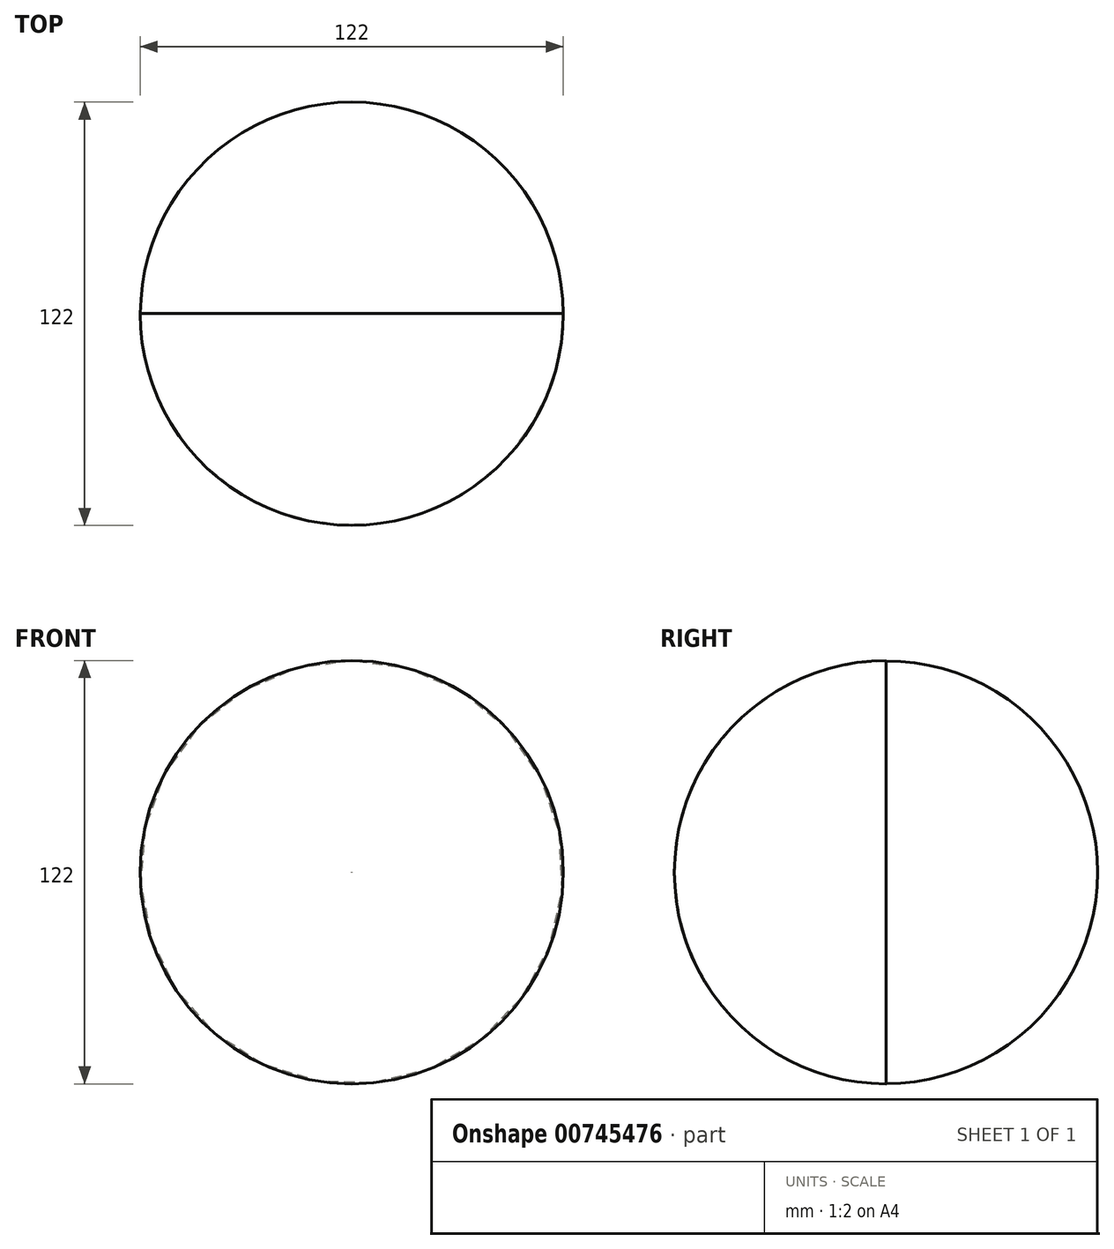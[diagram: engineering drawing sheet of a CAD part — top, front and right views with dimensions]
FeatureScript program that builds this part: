
annotation { "Feature Type Name" : "Feature", "Feature Type Description" : "" }
export const myFeature = defineFeature(function(context is Context, id is Id, definition is map)
    precondition{}
    {
        {
            var Q0;
            Q0=qCreatedBy(makeId("Front.planeOp"),FACE);
            var sketch = newSketch(context, id + "F0", { "sketchPlane" : qUnion([Q0])});
            skCircle(sketch, "E0", {"center": v(0, 0) * mm, "radius": 61 * mm});
            skSolve(sketch);
        }
        {
            var Q0;
            Q0 = qSketchRegion(id + "F0", true);
            extrude(context, id + "F1", {"entities" : qUnion([Q0]), "depth" : 122 * mm, "offsetDistance" : 25.4 * mm});
        }
        {
            var Q0;
            Q0=makeQuery(id+"F1.opExtrude","CAP_EDGE",EDGE,{"disambiguationData":[OSD([sQuery(id+"F0.wireOp",EDGE,"E0")])],"isStart":false});
            fillet(context, id + "F2", {"entities" : qUnion([Q0]), "radius" : 61 * mm, "tangentPropagation" : true, "allowEdgeOverflow" : false});
        }
        {
            var Q0;
            Q0=makeQuery(id+"F1.opExtrude","CAP_EDGE",EDGE,{"disambiguationData":[OSD([sQuery(id+"F0.wireOp",EDGE,"E0")])],"isStart":true});
            fillet(context, id + "F3", {"entities" : qUnion([Q0]), "radius" : 60.96 * mm, "tangentPropagation" : true, "allowEdgeOverflow" : false});
        }
    });
